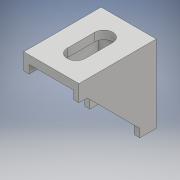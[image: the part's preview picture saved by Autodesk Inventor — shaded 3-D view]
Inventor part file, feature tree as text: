
AUTODESK INVENTOR PART (.ipt)
format: ipt  version: 2017 (Build 210142000, 142)  size: 150,016 bytes
history: native  units: mm
features: extrude x5, sketch x5, mirror x1
ambient origin geometry x8: Origin, YZ Plane, XZ Plane, XY Plane, X Axis, Y Axis, Z Axis, Center Point
bodies: Solid1 (feature_tree)
feature tree (11):
  extrude  "Extrusion1"  Depth=28.0mm
  extrude  "Extrusion2"  Depth=20.0mm
  extrude  "Extrusion3"  Depth=25.0mm TaperAngle=0.0deg
  mirror  "Mirror1"
  extrude  "Extrusion4"  Depth=3.0mm
  extrude  "Extrusion5"  Depth=3.0mm
  sketch  "Sketch1"  dims[d0=20.0mm d1=28.0mm]
  sketch  "Sketch2"  dims[d2=3.0mm d3=0.0mm d4=20.0mm]
  sketch  "Sketch3"  dims[d5=3.0mm d6=25.0mm d7=0.0mm]
  sketch  "Sketch4"  dims[d8=3.0mm d9=3.0mm]
  sketch  "Sketch5"  dims[d10=3.0mm d11=3.0mm d12=2.0mm d13=0.0mm d14=6.5mm d15=10.0mm d16=2.0mm d17=0.0mm d18=6.5mm d19=10.0mm d20=2.0mm d21=0.0mm]
